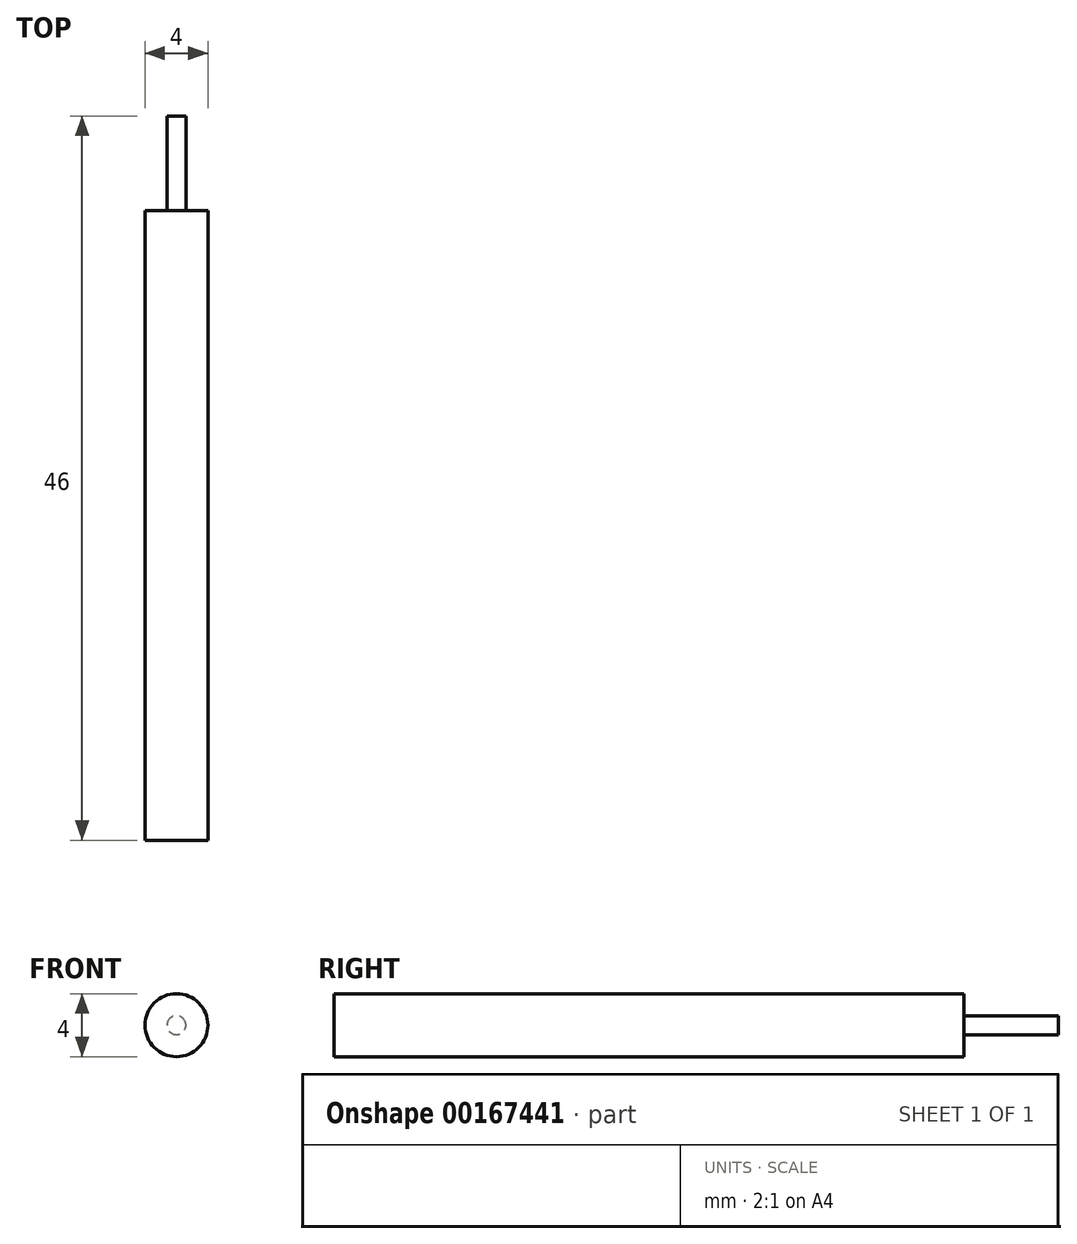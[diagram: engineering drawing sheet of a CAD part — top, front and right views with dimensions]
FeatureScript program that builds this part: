
annotation { "Feature Type Name" : "Feature", "Feature Type Description" : "" }
export const myFeature = defineFeature(function(context is Context, id is Id, definition is map)
    precondition{}
    {
        {
            var Q0;
            Q0=qCreatedBy(makeId("Front.planeOp"),FACE);
            var sketch = newSketch(context, id + "F0", { "sketchPlane" : qUnion([Q0])});
            skCircle(sketch, "E0", {"center": v(0, 0) * mm, "radius": 2 * mm});
            skSolve(sketch);
        }
        {
            var Q0;
            Q0=makeQuery(id+"F0.imprint","IMPRINT",FACE,{"disambiguationData":[TD([[makeQuery(id+"F0.imprint","IMPRINT",EDGE,{"derivedFrom":sQuery(id+"F0.wireOp",EDGE,"E0")}),1.0]])]});
            extrude(context, id + "F1", {"entities" : qUnion([Q0]), "oppositeDirection" : true, "depth" : 40 * mm});
        }
        {
            var Q0;
            Q0=makeQuery(id+"F1.opExtrude","CAP_FACE",FACE,{"disambiguationData":[OSD([sQuery(id+"F0.wireOp",EDGE,"E0")])],"isStart":false});
            var sketch = newSketch(context, id + "F2", { "sketchPlane" : qUnion([Q0])});
            skCircle(sketch, "E1", {"center": v(0, 0) * mm, "radius": 0.6 * mm});
            skSolve(sketch);
        }
        {
            var Q0;
            Q0=makeQuery(id+"F2.imprint","IMPRINT",FACE,{"disambiguationData":[TD([[makeQuery(id+"F2.imprint","IMPRINT",EDGE,{"derivedFrom":sQuery(id+"F2.wireOp",EDGE,"E1")}),1.0]])]});
            extrude(context, id + "F3", {"entities" : qUnion([Q0]), "operationType" : NewBodyOperationType.ADD, "depth" : 6 * mm});
        }
    });
